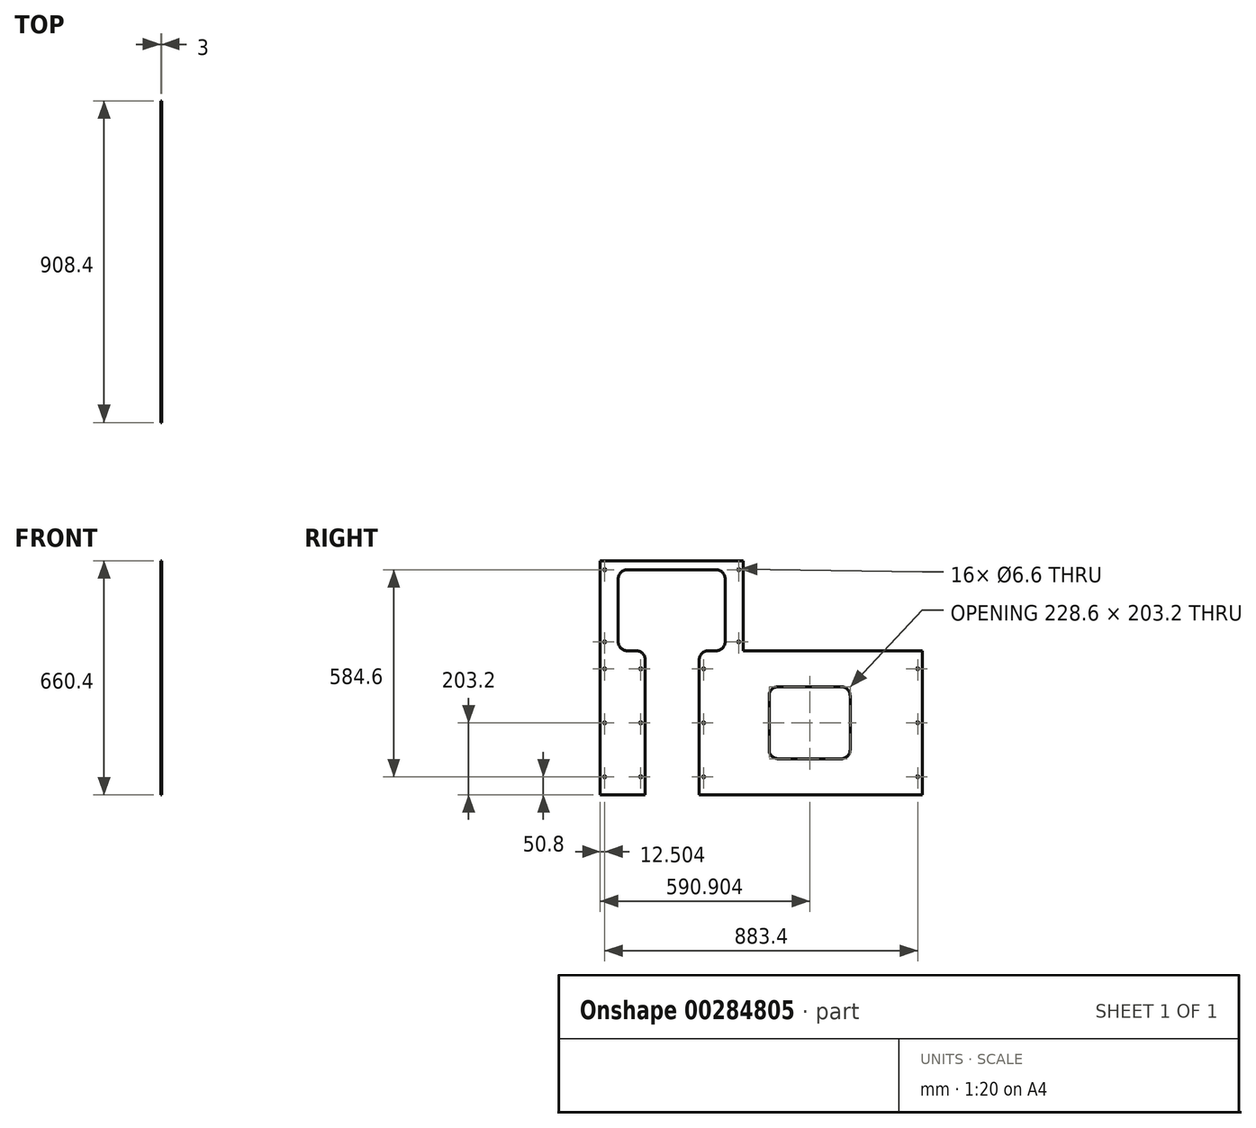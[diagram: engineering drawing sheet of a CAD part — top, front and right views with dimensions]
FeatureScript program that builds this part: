
annotation { "Feature Type Name" : "Feature", "Feature Type Description" : "" }
export const myFeature = defineFeature(function(context is Context, id is Id, definition is map)
    precondition{}
    {
        {
            var Q0;
            Q0=qCreatedBy(makeId("Right.planeOp"),FACE);
            var sketch = newSketch(context, id + "F0", { "sketchPlane" : qUnion([Q0])});
            skLineSegment(sketch, "E0.bottom", {"start": v(-588.3, 355.6) * mm, "end": v(-184.9, 355.6) * mm});
            skLineSegment(sketch, "E0.top", {"start": v(-588.3, -304.8) * mm, "end": v(-461.3, -304.8) * mm});
            skLineSegment(sketch, "E0.left", {"start": v(-588.3, 355.6) * mm, "end": v(-588.3, -304.8) * mm});
            skLineSegment(sketch, "E0.right", {"start": v(-184.9, 355.6) * mm, "end": v(-184.9, 101.6) * mm});
            skLineSegment(sketch, "E1.bottom", {"start": v(-184.9, 101.6) * mm, "end": v(320.1, 101.6) * mm});
            skLineSegment(sketch, "E1.top", {"start": v(-184.9, -304.8) * mm, "end": v(320.1, -304.8) * mm});
            skLineSegment(sketch, "E1.right", {"start": v(320.1, 101.6) * mm, "end": v(320.1, -304.8) * mm});
            skLineSegment(sketch, "E2.bottom", {"start": v(-512.1, 330.2) * mm, "end": v(-261.1, 330.2) * mm});
            skLineSegment(sketch, "E2.top", {"start": v(-512.1, 101.6) * mm, "end": v(-486.7, 101.6) * mm});
            skLineSegment(sketch, "E2.left", {"start": v(-537.5, 304.8) * mm, "end": v(-537.5, 127) * mm});
            skLineSegment(sketch, "E2.right", {"start": v(-235.7, 304.8) * mm, "end": v(-235.7, 127) * mm});
            skLineSegment(sketch, "E3.left", {"start": v(-461.3, 76.2) * mm, "end": v(-461.3, -304.8) * mm});
            skLineSegment(sketch, "E3.right", {"start": v(-308.9, 76.2) * mm, "end": v(-308.9, -304.8) * mm});
            skLineSegment(sketch, "E4.trimOffspring", {"start": v(-308.9, -304.8) * mm, "end": v(-184.9, -304.8) * mm});
            skLineSegment(sketch, "E5.trimOffspring", {"start": v(-283.5, 101.6) * mm, "end": v(-261.1, 101.6) * mm});
            skPoint(sketch, "E6.visualSharp", {"position": v(-235.7, 101.6) * mm});
            skArc(sketch, "E6.filletArc", {"start": v(-261.1, 101.6) * mm, "mid": v(-243.15, 109.04) * mm, "end": v(-235.7, 127) * mm});
            skPoint(sketch, "E7.visualSharp", {"position": v(-308.9, 101.6) * mm});
            skArc(sketch, "E7.filletArc", {"start": v(-283.5, 101.6) * mm, "mid": v(-301.47, 94.16) * mm, "end": v(-308.9, 76.2) * mm});
            skPoint(sketch, "E8.visualSharp", {"position": v(-235.7, 330.2) * mm});
            skArc(sketch, "E8.filletArc", {"start": v(-235.7, 304.8) * mm, "mid": v(-243.15, 322.76) * mm, "end": v(-261.1, 330.2) * mm});
            skPoint(sketch, "E9.visualSharp", {"position": v(-537.5, 330.2) * mm});
            skArc(sketch, "E9.filletArc", {"start": v(-512.1, 330.2) * mm, "mid": v(-530.07, 322.76) * mm, "end": v(-537.5, 304.8) * mm});
            skPoint(sketch, "E10.visualSharp", {"position": v(-537.5, 101.6) * mm});
            skArc(sketch, "E10.filletArc", {"start": v(-537.5, 127) * mm, "mid": v(-530.07, 109.04) * mm, "end": v(-512.1, 101.6) * mm});
            skPoint(sketch, "E11.visualSharp", {"position": v(-461.3, 101.6) * mm});
            skArc(sketch, "E11.filletArc", {"start": v(-461.3, 76.2) * mm, "mid": v(-468.75, 94.16) * mm, "end": v(-486.7, 101.6) * mm});
            skLineSegment(sketch, "E12.bottom", {"start": v(-86.3, 0) * mm, "end": v(91.5, 0) * mm});
            skLineSegment(sketch, "E12.top", {"start": v(-86.3, -203.2) * mm, "end": v(91.5, -203.2) * mm});
            skLineSegment(sketch, "E12.left", {"start": v(-111.7, -25.4) * mm, "end": v(-111.7, -177.8) * mm});
            skLineSegment(sketch, "E12.right", {"start": v(116.9, -25.4) * mm, "end": v(116.9, -177.8) * mm});
            skPoint(sketch, "E13.visualSharp", {"position": v(-111.7, 0) * mm});
            skArc(sketch, "E13.filletArc", {"start": v(-86.3, 0) * mm, "mid": v(-104.27, -7.44) * mm, "end": v(-111.7, -25.4) * mm});
            skPoint(sketch, "E14.visualSharp", {"position": v(116.9, 0) * mm});
            skArc(sketch, "E14.filletArc", {"start": v(116.9, -25.4) * mm, "mid": v(109.45, -7.44) * mm, "end": v(91.5, 0) * mm});
            skPoint(sketch, "E15.visualSharp", {"position": v(116.9, -203.2) * mm});
            skArc(sketch, "E15.filletArc", {"start": v(91.5, -203.2) * mm, "mid": v(109.45, -195.76) * mm, "end": v(116.9, -177.8) * mm});
            skPoint(sketch, "E16.visualSharp", {"position": v(-111.7, -203.2) * mm});
            skArc(sketch, "E16.filletArc", {"start": v(-111.7, -177.8) * mm, "mid": v(-104.27, -195.76) * mm, "end": v(-86.3, -203.2) * mm});
            skSolve(sketch);
        }
        {
            var Q0;
            Q0 = qSketchRegion(id + "F0", true);
            extrude(context, id + "F1", {"entities" : qUnion([Q0]), "depth" : 3 * mm});
        }
        {
            var Q0;
            Q0=makeQuery(id+"F1.opExtrude","CAP_FACE",FACE,{"disambiguationData":[OSD([sQuery(id+"F0.wireOp",EDGE,"E0.bottom"),sQuery(id+"F0.wireOp",EDGE,"E0.top"),sQuery(id+"F0.wireOp",EDGE,"E0.left"),sQuery(id+"F0.wireOp",EDGE,"E0.right"),sQuery(id+"F0.wireOp",EDGE,"E1.bottom"),sQuery(id+"F0.wireOp",EDGE,"E1.top"),sQuery(id+"F0.wireOp",EDGE,"E1.right"),sQuery(id+"F0.wireOp",EDGE,"E2.bottom"),sQuery(id+"F0.wireOp",EDGE,"E2.top"),sQuery(id+"F0.wireOp",EDGE,"E2.left"),sQuery(id+"F0.wireOp",EDGE,"E2.right"),sQuery(id+"F0.wireOp",EDGE,"E3.left"),sQuery(id+"F0.wireOp",EDGE,"E3.right"),sQuery(id+"F0.wireOp",EDGE,"E4.trimOffspring"),sQuery(id+"F0.wireOp",EDGE,"E5.trimOffspring"),sQuery(id+"F0.wireOp",EDGE,"E6.filletArc"),sQuery(id+"F0.wireOp",EDGE,"E7.filletArc"),sQuery(id+"F0.wireOp",EDGE,"E8.filletArc"),sQuery(id+"F0.wireOp",EDGE,"E9.filletArc"),sQuery(id+"F0.wireOp",EDGE,"E10.filletArc"),sQuery(id+"F0.wireOp",EDGE,"E11.filletArc"),sQuery(id+"F0.wireOp",EDGE,"E12.bottom"),sQuery(id+"F0.wireOp",EDGE,"E12.top"),sQuery(id+"F0.wireOp",EDGE,"E12.left"),sQuery(id+"F0.wireOp",EDGE,"E12.right"),sQuery(id+"F0.wireOp",EDGE,"E13.filletArc"),sQuery(id+"F0.wireOp",EDGE,"E14.filletArc"),sQuery(id+"F0.wireOp",EDGE,"E15.filletArc"),sQuery(id+"F0.wireOp",EDGE,"E16.filletArc")])],"isStart":false});
            var sketch = newSketch(context, id + "F2", { "sketchPlane" : qUnion([Q0])});
            skPoint(sketch, "E17", {"position": v(-575.8, -254) * mm});
            skPoint(sketch, "E18", {"position": v(-575.8, -101.6) * mm});
            skPoint(sketch, "E19", {"position": v(-575.8, 50.8) * mm});
            skPoint(sketch, "E20", {"position": v(-575.8, 126.6) * mm});
            skPoint(sketch, "E21", {"position": v(-575.8, 330.6) * mm});
            skPoint(sketch, "E22", {"position": v(-197.4, 330.6) * mm});
            skPoint(sketch, "E23", {"position": v(-197.4, 126.6) * mm});
            skPoint(sketch, "E24", {"position": v(307.6, 50.8) * mm});
            skPoint(sketch, "E25", {"position": v(307.6, -101.6) * mm});
            skPoint(sketch, "E26", {"position": v(307.6, -254) * mm});
            skPoint(sketch, "E27", {"position": v(-296.4, 50.8) * mm});
            skPoint(sketch, "E28", {"position": v(-296.4, -101.6) * mm});
            skPoint(sketch, "E29", {"position": v(-296.4, -254) * mm});
            skPoint(sketch, "E30", {"position": v(-473.8, 50.8) * mm});
            skPoint(sketch, "E31", {"position": v(-473.8, -101.6) * mm});
            skPoint(sketch, "E32", {"position": v(-473.8, -254) * mm});
            skSolve(sketch);
        }
        {
            var Q0;
            Q0=sQuery(id+"F2.wireOp",VERTEX,"E19");
            var Q1;
            Q1=sQuery(id+"F2.wireOp",VERTEX,"E20");
            var Q2;
            Q2=sQuery(id+"F2.wireOp",VERTEX,"E21");
            var Q3;
            Q3=sQuery(id+"F2.wireOp",VERTEX,"E18");
            var Q4;
            Q4=sQuery(id+"F2.wireOp",VERTEX,"E17");
            var Q5;
            Q5=sQuery(id+"F2.wireOp",VERTEX,"E31");
            var Q6;
            Q6=sQuery(id+"F2.wireOp",VERTEX,"E30");
            var Q7;
            Q7=sQuery(id+"F2.wireOp",VERTEX,"E22");
            var Q8;
            Q8=sQuery(id+"F2.wireOp",VERTEX,"E23");
            var Q9;
            Q9=sQuery(id+"F2.wireOp",VERTEX,"E27");
            var Q10;
            Q10=sQuery(id+"F2.wireOp",VERTEX,"E28");
            var Q11;
            Q11=sQuery(id+"F2.wireOp",VERTEX,"E29");
            var Q12;
            Q12=sQuery(id+"F2.wireOp",VERTEX,"E24");
            var Q13;
            Q13=sQuery(id+"F2.wireOp",VERTEX,"E25");
            var Q14;
            Q14=sQuery(id+"F2.wireOp",VERTEX,"E26");
            var Q15;
            Q15=sQuery(id+"F2.wireOp",VERTEX,"E32");
            var Q16;
            Q16=makeQuery(id+"F1.opExtrude","SWEPT_BODY",BODY,{"disambiguationData":[OSD([sQuery(id+"F0.wireOp",EDGE,"E0.bottom"),sQuery(id+"F0.wireOp",EDGE,"E0.top"),sQuery(id+"F0.wireOp",EDGE,"E0.left"),sQuery(id+"F0.wireOp",EDGE,"E0.right"),sQuery(id+"F0.wireOp",EDGE,"E1.bottom"),sQuery(id+"F0.wireOp",EDGE,"E1.top"),sQuery(id+"F0.wireOp",EDGE,"E1.right"),sQuery(id+"F0.wireOp",EDGE,"E2.bottom"),sQuery(id+"F0.wireOp",EDGE,"E2.top"),sQuery(id+"F0.wireOp",EDGE,"E2.left"),sQuery(id+"F0.wireOp",EDGE,"E2.right"),sQuery(id+"F0.wireOp",EDGE,"E3.left"),sQuery(id+"F0.wireOp",EDGE,"E3.right"),sQuery(id+"F0.wireOp",EDGE,"E4.trimOffspring"),sQuery(id+"F0.wireOp",EDGE,"E5.trimOffspring"),sQuery(id+"F0.wireOp",EDGE,"E6.filletArc"),sQuery(id+"F0.wireOp",EDGE,"E7.filletArc"),sQuery(id+"F0.wireOp",EDGE,"E8.filletArc"),sQuery(id+"F0.wireOp",EDGE,"E9.filletArc"),sQuery(id+"F0.wireOp",EDGE,"E10.filletArc"),sQuery(id+"F0.wireOp",EDGE,"E11.filletArc"),sQuery(id+"F0.wireOp",EDGE,"E12.bottom"),sQuery(id+"F0.wireOp",EDGE,"E12.top"),sQuery(id+"F0.wireOp",EDGE,"E12.left"),sQuery(id+"F0.wireOp",EDGE,"E12.right"),sQuery(id+"F0.wireOp",EDGE,"E13.filletArc"),sQuery(id+"F0.wireOp",EDGE,"E14.filletArc"),sQuery(id+"F0.wireOp",EDGE,"E15.filletArc"),sQuery(id+"F0.wireOp",EDGE,"E16.filletArc")])]});
            hole(context, id + "F3", {"style" : HoleStyle.SIMPLE, "endStyle" : HoleEndStyle.THROUGH, "standardTappedOrClearance" : lookupTablePath({ "standard" : "ISO", "fit" : "Normal", "size" : "M6", "type" : "Clearance" }), "standardBlindInLast" : lookupTablePath({ "fit" : "Standard", "standard" : "ISO", "size" : "M6", "type" : "Clearance" }), "holeDiameter" : 6.6 * mm, "tappedDepth" : 12 * mm, "tapClearance" : 3, "locations" : qUnion([Q0, Q1, Q2, Q3, Q4, Q5, Q6, Q7, Q8, Q9, Q10, Q11, Q12, Q13, Q14, Q15]), "scope" : qUnion([Q16])});
        }
    });
